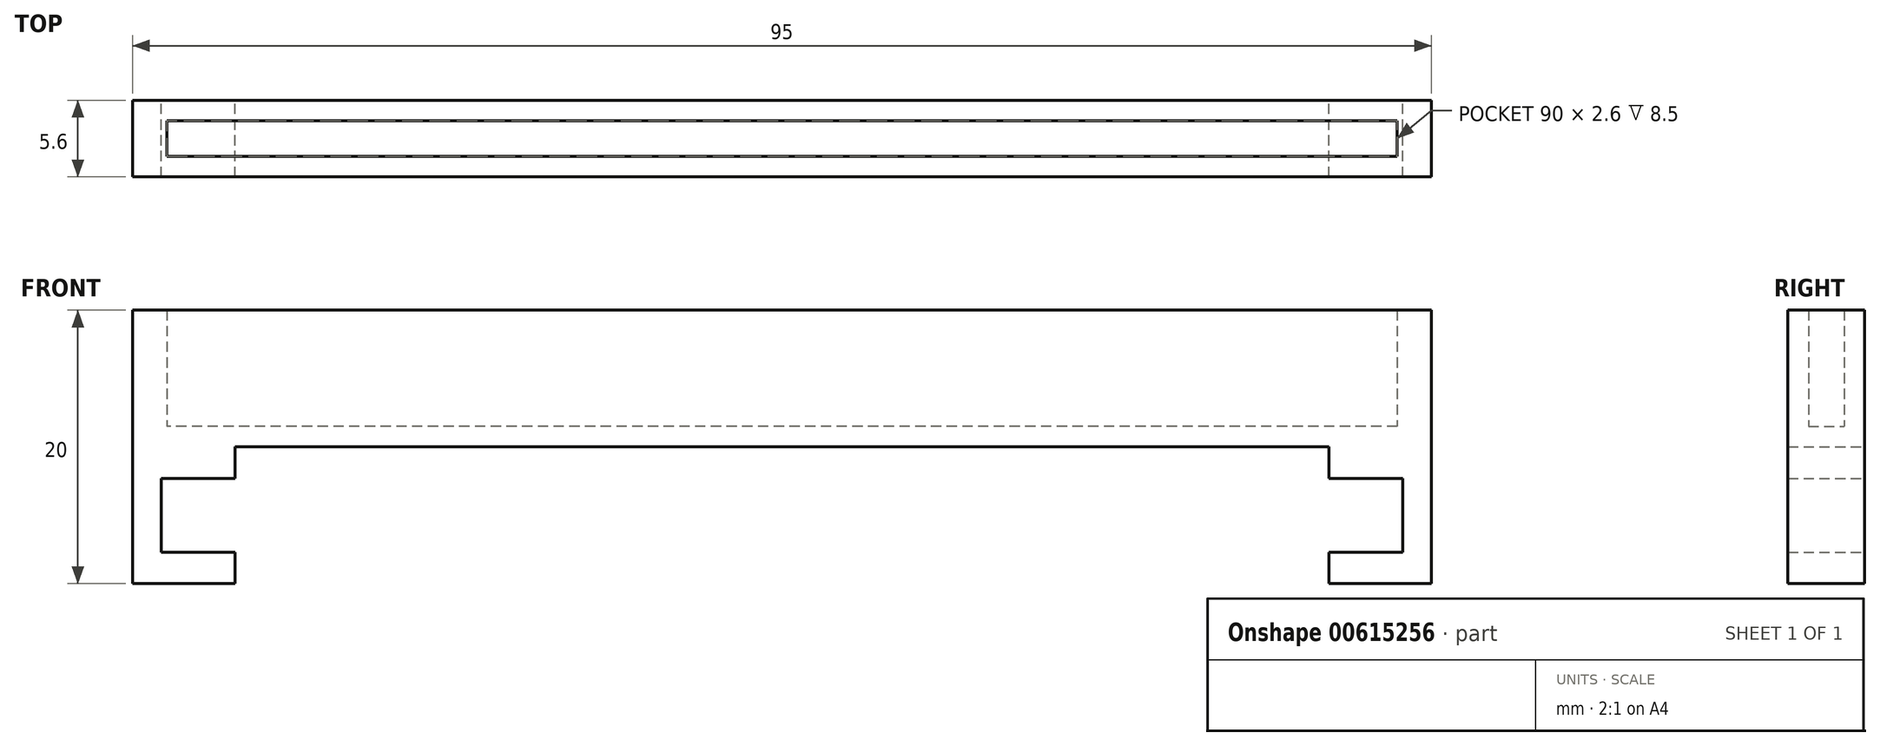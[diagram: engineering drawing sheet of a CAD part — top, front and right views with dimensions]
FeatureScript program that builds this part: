
annotation { "Feature Type Name" : "Feature", "Feature Type Description" : "" }
export const myFeature = defineFeature(function(context is Context, id is Id, definition is map)
    precondition{}
    {
        {
            var Q0;
            Q0=qCreatedBy(makeId("Top.planeOp"),FACE);
            var sketch = newSketch(context, id + "F0", { "sketchPlane" : qUnion([Q0])});
            skLineSegment(sketch, "E0.bottom", {"start": v(47.5, -2.8) * mm, "end": v(-47.5, -2.8) * mm});
            skLineSegment(sketch, "E0.top", {"start": v(47.5, 2.8) * mm, "end": v(-47.5, 2.8) * mm});
            skLineSegment(sketch, "E0.left", {"start": v(47.5, -2.8) * mm, "end": v(47.5, 2.8) * mm});
            skLineSegment(sketch, "E0.right", {"start": v(-47.5, -2.8) * mm, "end": v(-47.5, 2.8) * mm});
            skPoint(sketch, "E0.middle", {"position": v(0, 0) * mm});
            skLineSegment(sketch, "E1.bottom", {"start": v(45, -1.3) * mm, "end": v(-45, -1.3) * mm});
            skLineSegment(sketch, "E1.top", {"start": v(45, 1.3) * mm, "end": v(-45, 1.3) * mm});
            skLineSegment(sketch, "E1.left", {"start": v(45, -1.3) * mm, "end": v(45, 1.3) * mm});
            skLineSegment(sketch, "E1.right", {"start": v(-45, -1.3) * mm, "end": v(-45, 1.3) * mm});
            skSolve(sketch);
        }
        {
            var Q0;
            Q0=makeQuery(id+"F0.imprint","IMPRINT",FACE,{"disambiguationData":[TD([[makeQuery(id+"F0.imprint","IMPRINT",EDGE,{"derivedFrom":sQuery(id+"F0.wireOp",EDGE,"E0.bottom")}),-1.0]])]});
            extrude(context, id + "F1", {"entities" : qUnion([Q0]), "depth" : 10 * mm, "offsetDistance" : 25 * mm});
        }
        {
            var Q0;
            Q0=makeQuery(id+"F0.imprint","IMPRINT",FACE,{"disambiguationData":[TD([[makeQuery(id+"F0.imprint","IMPRINT",EDGE,{"derivedFrom":sQuery(id+"F0.wireOp",EDGE,"E1.bottom")}),-1.0]])]});
            extrude(context, id + "F2", {"entities" : qUnion([Q0]), "operationType" : NewBodyOperationType.ADD, "depth" : 1.5 * mm, "offsetDistance" : 25 * mm});
        }
        {
            var Q0;
            Q0=makeQuery(id+"F1.opExtrude","SWEPT_FACE",FACE,{"disambiguationData":[OSD([sQuery(id+"F0.wireOp",EDGE,"E0.top")])]});
            var sketch = newSketch(context, id + "F3", { "sketchPlane" : qUnion([Q0])});
            skLineSegment(sketch, "E2", {"start": v(0, 0) * mm, "end": v(0, 5) * mm});
            skLineSegment(sketch, "E3.bottom", {"start": v(40, 0) * mm, "end": v(-40, 0) * mm});
            skLineSegment(sketch, "E3.top", {"start": v(40, 10) * mm, "end": v(-40, 10) * mm});
            skLineSegment(sketch, "E3.left", {"start": v(40, 0) * mm, "end": v(40, 10) * mm});
            skLineSegment(sketch, "E3.right", {"start": v(-40, 0) * mm, "end": v(-40, 10) * mm});
            skPoint(sketch, "E3.middle", {"position": v(0, 5) * mm});
            skLineSegment(sketch, "E4.bottom", {"start": v(-40, 7.7) * mm, "end": v(-45.4, 7.7) * mm});
            skLineSegment(sketch, "E4.top", {"start": v(-40, 2.3) * mm, "end": v(-45.4, 2.3) * mm});
            skLineSegment(sketch, "E4.left", {"start": v(-40, 7.7) * mm, "end": v(-40, 2.3) * mm});
            skLineSegment(sketch, "E4.right", {"start": v(-45.4, 7.7) * mm, "end": v(-45.4, 2.3) * mm});
            skLineSegment(sketch, "E5.bottom", {"start": v(-40, 10) * mm, "end": v(-38, 10) * mm});
            skLineSegment(sketch, "E5.top", {"start": v(-40, 0) * mm, "end": v(-38, 0) * mm});
            skLineSegment(sketch, "E5.left", {"start": v(-40, 10) * mm, "end": v(-40, 0) * mm});
            skLineSegment(sketch, "E5.right", {"start": v(-38, 10) * mm, "end": v(-38, 0) * mm});
            skLineSegment(sketch, "E6.MirrorCS", {"start": v(40, 7.7) * mm, "end": v(40, 2.3) * mm});
            skLineSegment(sketch, "E7.MirrorCS", {"start": v(40, 7.7) * mm, "end": v(45.4, 7.7) * mm});
            skLineSegment(sketch, "E8.MirrorCS", {"start": v(40, 2.3) * mm, "end": v(45.4, 2.3) * mm});
            skLineSegment(sketch, "E9.MirrorCS", {"start": v(40, 10) * mm, "end": v(38, 10) * mm});
            skLineSegment(sketch, "E10.MirrorCS", {"start": v(40, 0) * mm, "end": v(38, 0) * mm});
            skLineSegment(sketch, "E11.MirrorCS", {"start": v(40, 10) * mm, "end": v(40, 0) * mm});
            skLineSegment(sketch, "E12.MirrorCS", {"start": v(45.4, 7.7) * mm, "end": v(45.4, 2.3) * mm});
            skLineSegment(sketch, "E13.MirrorCS", {"start": v(38, 10) * mm, "end": v(38, 0) * mm});
            skLineSegment(sketch, "E14.MirrorCS", {"start": v(-40, -7.7) * mm, "end": v(-45.4, -7.7) * mm});
            skLineSegment(sketch, "E15.MirrorCS", {"start": v(-45.4, -7.7) * mm, "end": v(-45.4, -2.3) * mm});
            skLineSegment(sketch, "E16.MirrorCS", {"start": v(-40, -2.3) * mm, "end": v(-45.4, -2.3) * mm});
            skLineSegment(sketch, "E17.MirrorCS", {"start": v(-40, -10) * mm, "end": v(-40, 0) * mm});
            skLineSegment(sketch, "E18.MirrorCS", {"start": v(-38, -10) * mm, "end": v(-38, 0) * mm});
            skLineSegment(sketch, "E19.MirrorCS", {"start": v(40, -10) * mm, "end": v(-40, -10) * mm});
            skLineSegment(sketch, "E20.MirrorCS", {"start": v(38, -10) * mm, "end": v(38, 0) * mm});
            skLineSegment(sketch, "E21.MirrorCS", {"start": v(40, -10) * mm, "end": v(40, 0) * mm});
            skLineSegment(sketch, "E22.MirrorCS", {"start": v(40, -2.3) * mm, "end": v(45.4, -2.3) * mm});
            skLineSegment(sketch, "E23.MirrorCS", {"start": v(45.4, -7.7) * mm, "end": v(45.4, -2.3) * mm});
            skLineSegment(sketch, "E24.MirrorCS", {"start": v(40, -7.7) * mm, "end": v(40, -2.3) * mm});
            skLineSegment(sketch, "E25.MirrorCS", {"start": v(40, -7.7) * mm, "end": v(45.4, -7.7) * mm});
            skLineSegment(sketch, "E26.bottom", {"start": v(-47.5, 0) * mm, "end": v(-40, 0) * mm});
            skLineSegment(sketch, "E26.top", {"start": v(-47.5, -10) * mm, "end": v(-40, -10) * mm});
            skLineSegment(sketch, "E26.left", {"start": v(-47.5, 0) * mm, "end": v(-47.5, -10) * mm});
            skLineSegment(sketch, "E26.right", {"start": v(-40, 0) * mm, "end": v(-40, -10) * mm});
            skLineSegment(sketch, "E27.bottom", {"start": v(40, -10) * mm, "end": v(47.5, -10) * mm});
            skLineSegment(sketch, "E27.top", {"start": v(40, 0) * mm, "end": v(47.5, 0) * mm});
            skLineSegment(sketch, "E27.right", {"start": v(47.5, -10) * mm, "end": v(47.5, 0) * mm});
            skSolve(sketch);
        }
        {
            var Q0;
            {var subQ2=sQuery(id+"F3.wireOp",EDGE,"E14.MirrorCS");Q0=makeQuery(id+"F3.imprint","IMPRINT",FACE,{"disambiguationData":[TD([[makeQuery(id+"F3.imprint","IMPRINT",EDGE,{"derivedFrom":subQ2}),1.0]])]});}
            var Q1;
            {var subQ1=sQuery(id+"F3.wireOp",EDGE,"E5.top");Q1=makeQuery(id+"F3.imprint","IMPRINT",FACE,{"disambiguationData":[TD([[makeQuery(id+"F3.imprint","IMPRINT",EDGE,{"derivedFrom":subQ1}),-1.0]])]});}
            var Q2;
            {var subQ5=sQuery(id+"F3.wireOp",EDGE,"E10.MirrorCS");Q2=makeQuery(id+"F3.imprint","IMPRINT",FACE,{"disambiguationData":[TD([[makeQuery(id+"F3.imprint","IMPRINT",EDGE,{"derivedFrom":subQ5}),-1.0]])]});}
            var Q3;
            {var subQ4=sQuery(id+"F3.wireOp",EDGE,"E22.MirrorCS");Q3=makeQuery(id+"F3.imprint","IMPRINT",FACE,{"disambiguationData":[TD([[makeQuery(id+"F3.imprint","IMPRINT",EDGE,{"derivedFrom":subQ4}),1.0]])]});}
            extrude(context, id + "F4", {"entities" : qUnion([Q0, Q1, Q2, Q3]), "operationType" : NewBodyOperationType.ADD, "oppositeDirection" : true, "depth" : 5.6 * mm, "offsetDistance" : 25 * mm});
        }
    });
